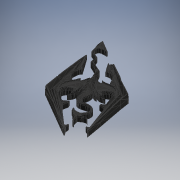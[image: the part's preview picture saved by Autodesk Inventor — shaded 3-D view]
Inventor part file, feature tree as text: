
AUTODESK INVENTOR PART (.ipt)
format: ipt  version: 2018 (Build 220112000, 112)  size: 5,880,832 bytes
history: native  units: mm
features: other x4, extrude x1, sketch x1
ambient origin geometry x8: Origin, YZ Plane, XZ Plane, XY Plane, X Axis, Y Axis, Z Axis, Center Point
bodies: Body1 (feature_tree)
feature tree (6):
  other  "skyrimlogo2.ipt"
  extrude  "押し出し1"  Depth=0.769231mm
  other  "ソリッド1::skyrimlogo2.ipt"
  other  "TaggingFeature1"
  sketch  "スケッチ1"
  other  "ソリッド1"
